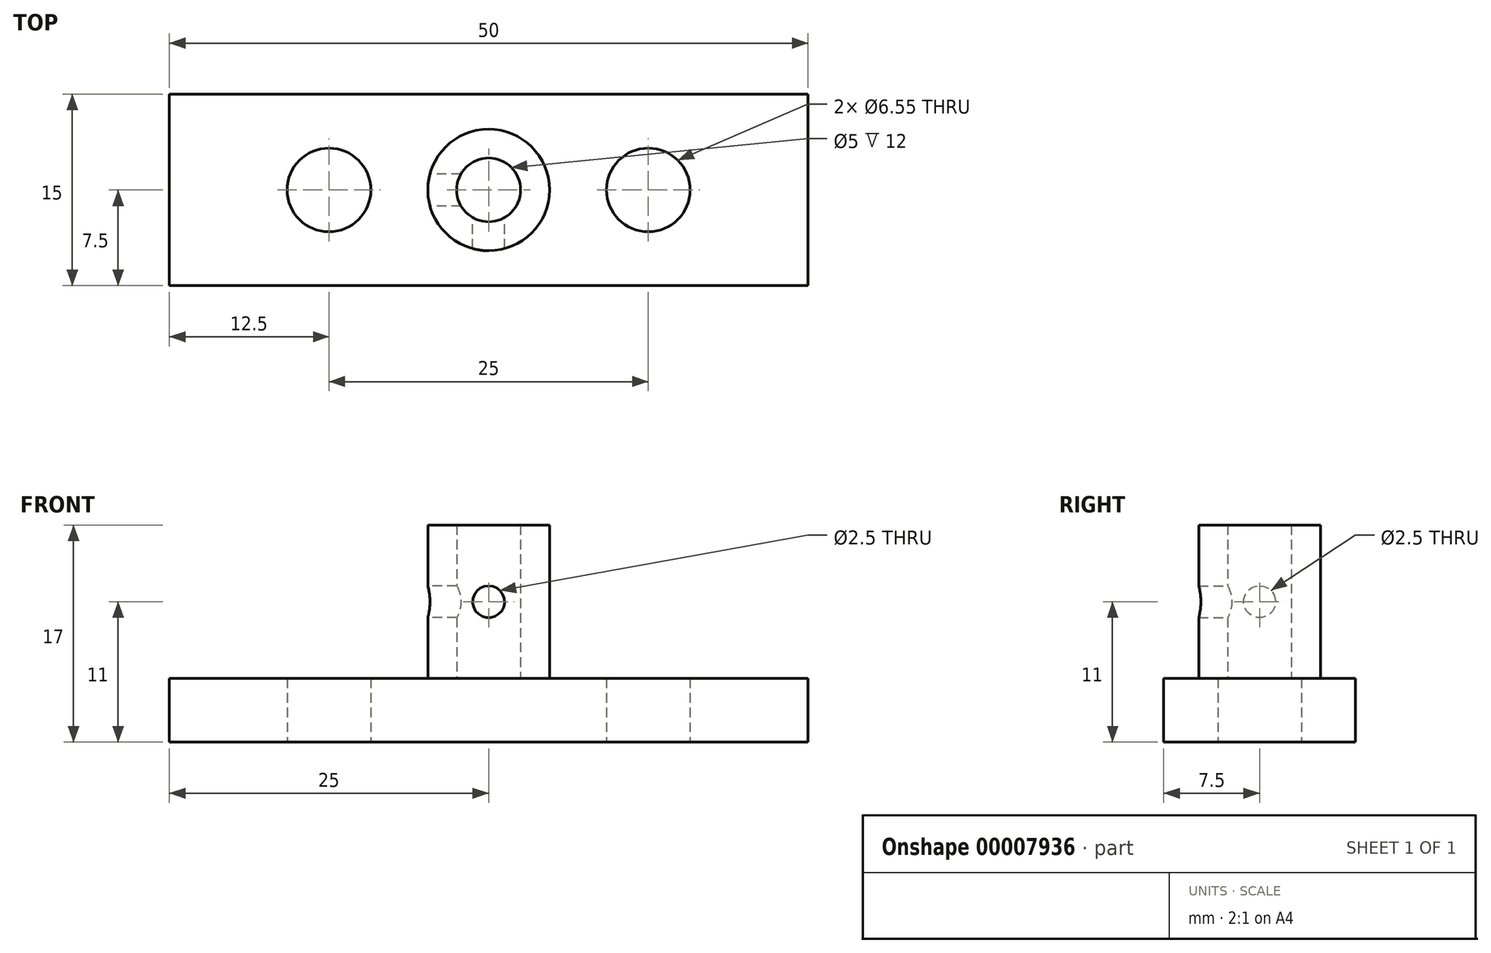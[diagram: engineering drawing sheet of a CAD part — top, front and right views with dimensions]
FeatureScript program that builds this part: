
annotation { "Feature Type Name" : "Feature", "Feature Type Description" : "" }
export const myFeature = defineFeature(function(context is Context, id is Id, definition is map)
    precondition{}
    {
        {
            var Q0;
            Q0=qCreatedBy(makeId("Top.planeOp"),FACE);
            var sketch = newSketch(context, id + "F0", { "sketchPlane" : qUnion([Q0])});
            skCircle(sketch, "E0", {"center": v(0, 0) * mm, "radius": 4.76 * mm});
            skCircle(sketch, "E1", {"center": v(0, 0) * mm, "radius": 2.5 * mm});
            skLineSegment(sketch, "E2.rect.bottom", {"start": v(-25, 7.5) * mm, "end": v(25, 7.5) * mm});
            skLineSegment(sketch, "E2.rect.top", {"start": v(-25, -7.5) * mm, "end": v(25, -7.5) * mm});
            skLineSegment(sketch, "E2.rect.left", {"start": v(-25, 7.5) * mm, "end": v(-25, -7.5) * mm});
            skLineSegment(sketch, "E2.rect.right", {"start": v(25, 7.5) * mm, "end": v(25, -7.5) * mm});
            skLineSegment(sketch, "E3", {"start": v(-12.5, 0) * mm, "end": v(0, 0) * mm, "construction": true});
            skLineSegment(sketch, "E4", {"start": v(0, 0) * mm, "end": v(12.5, 0) * mm, "construction": true});
            skPoint(sketch, "E5", {"position": v(-12.5, 0) * mm});
            skPoint(sketch, "E6", {"position": v(12.5, 0) * mm});
            skLineSegment(sketch, "E7", {"start": v(0, 0) * mm, "end": v(0, -4.76) * mm, "construction": true});
            skSolve(sketch);
        }
        {
            var Q0;
            Q0=makeQuery(id+"F0.imprint","IMPRINT",FACE,{"disambiguationData":[TD([[makeQuery(id+"F0.imprint","IMPRINT",EDGE,{"derivedFrom":sQuery(id+"F0.wireOp",EDGE,"E0")}),1.0]])]});
            extrude(context, id + "F1", {"entities" : qUnion([Q0]), "depth" : 12 * mm});
        }
        {
            var Q0;
            Q0=makeQuery(id+"F0.imprint","IMPRINT",FACE,{"disambiguationData":[TD([[makeQuery(id+"F0.imprint","IMPRINT",EDGE,{"derivedFrom":sQuery(id+"F0.wireOp",EDGE,"E0")}),-1.0]])]});
            var Q1;
            Q1=makeQuery(id+"F0.imprint","IMPRINT",FACE,{"disambiguationData":[TD([[makeQuery(id+"F0.imprint","IMPRINT",EDGE,{"derivedFrom":sQuery(id+"F0.wireOp",EDGE,"E0")}),1.0]])]});
            var Q2;
            Q2=makeQuery(id+"F0.imprint","IMPRINT",FACE,{"disambiguationData":[TD([[makeQuery(id+"F0.imprint","IMPRINT",EDGE,{"derivedFrom":sQuery(id+"F0.wireOp",EDGE,"E1")}),1.0]])]});
            extrude(context, id + "F2", {"entities" : qUnion([Q0, Q1, Q2]), "operationType" : NewBodyOperationType.ADD, "oppositeDirection" : true, "depth" : 5 * mm});
        }
        {
            var Q0;
            Q0=sQuery(id+"F0.wireOp",VERTEX,"E5");
            var Q1;
            Q1=sQuery(id+"F0.wireOp",VERTEX,"E6");
            var Q2;
            Q2=makeQuery(id+"F1.opExtrude","SWEPT_BODY",BODY,{"disambiguationData":[OSD([sQuery(id+"F0.wireOp",EDGE,"E0"),sQuery(id+"F0.wireOp",EDGE,"E1")])]});
            hole(context, id + "F3", {"style" : HoleStyle.SIMPLE, "holeDiameter" : 6.35 * mm + 0.2 * mm, "endStyle" : HoleEndStyle.THROUGH, "locations" : qUnion([Q0, Q1]), "scope" : qUnion([Q2])});
        }
        {
            var Q0;
            Q0=qCreatedBy(makeId("Right.planeOp"),FACE);
            var sketch = newSketch(context, id + "F4", { "sketchPlane" : qUnion([Q0])});
            skPoint(sketch, "E8", {"position": v(0, 0) * mm});
            skLineSegment(sketch, "E9", {"start": v(0, 0) * mm, "end": v(0, 12) * mm, "construction": true});
            skPoint(sketch, "E10", {"position": v(0, 6) * mm});
            skSolve(sketch);
        }
        {
            var Q0;
            Q0=sQuery(id+"F4.wireOp",VERTEX,"E10");
            var Q1;
            Q1=makeQuery(id+"F1.opExtrude","SWEPT_BODY",BODY,{"disambiguationData":[OSD([sQuery(id+"F0.wireOp",EDGE,"E0"),sQuery(id+"F0.wireOp",EDGE,"E1")])]});
            hole(context, id + "F5", {"style" : HoleStyle.SIMPLE, "holeDiameter" : 2.5 * mm, "endStyle" : HoleEndStyle.THROUGH, "locations" : qUnion([Q0]), "scope" : qUnion([Q1])});
        }
        {
            var Q0;
            Q0=qCreatedBy(makeId("Front.planeOp"),FACE);
            var sketch = newSketch(context, id + "F6", { "sketchPlane" : qUnion([Q0])});
            skCircle(sketch, "E11", {"center": v(0, 6) * mm, "radius": 1.25 * mm});
            skSolve(sketch);
        }
        {
            var Q0;
            Q0=makeQuery(id+"F6.imprint","IMPRINT",FACE,{"disambiguationData":[TD([[makeQuery(id+"F6.imprint","IMPRINT",EDGE,{"derivedFrom":sQuery(id+"F6.wireOp",EDGE,"E11")}),1.0]])]});
            extrude(context, id + "F7", {"entities" : qUnion([Q0]), "operationType" : NewBodyOperationType.REMOVE, "endBound" : BoundingType.THROUGH_ALL, "depth" : 25 * mm});
        }
    });
